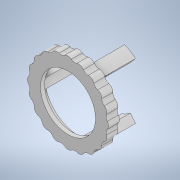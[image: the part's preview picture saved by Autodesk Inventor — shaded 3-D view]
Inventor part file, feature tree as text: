
AUTODESK INVENTOR PART (.ipt)
format: ipt  version: 2022 (Build 260153000, 153)  size: 384,512 bytes
history: native  units: in
note: dims shown in document units (in); Inventor stores cm internally (conversion verified against a paired STEP export)
features: thicken_offset x6, other x6, extrude x4, sketch x4, projected_geometry x4, plane x1, chamfer x1, fillet x1, reference x1
ambient origin geometry x8: Origin, YZ Plane, XZ Plane, XY Plane, X Axis, Y Axis, Z Axis, Center Point
bodies: Solid1 (feature_tree)
feature tree (28):
  extrude  "Extrusion1"  Depth=1.1681in
  plane  "Work Plane1"
  extrude  "Extrusion2"  Depth=0.481in
  extrude  "Extrusion3"  Depth=0.2in
  chamfer  "Chamfer1"  Distance=0.2in
  thicken_offset  "Thicken1"
  thicken_offset  "Thicken2"
  thicken_offset  "Thicken3"
  extrude  "Extrusion4"  Depth=0.6in TaperAngle=0.0deg
  fillet  "Fillet1"  Radius=1.315in
  thicken_offset  "Thicken4"
  thicken_offset  "Thicken5"
  thicken_offset  "Thicken6"
  sketch  "Sketch1"  dims[d0=1.1681in d1=1.1681in]
  reference  "Reference1"
  sketch  "Sketch3"  dims[d2=0.3436in d3=0.481in]
  sketch  "Sketch4"  dims[d4=0.3436in d5=0.481in d6=0.2in d7=0.0in]
  projected_geometry  "Projected Loop1"
  projected_geometry  "Projected Loop2"
  projected_geometry  "Projected Loop3"
  sketch  "Sketch5"  dims[d8=1.1681in d9=1.1681in d10=0.3436in d11=0.481in d12=0.3436in d13=0.481in d14=0.6in d15=0.0in d16=1.315in d17=1.025in d18=0.1181in d19=0.1181in d20=0.1181in d21=0.25in d22=0.0in d23=0.125in d24=0.125in d25=45.0deg d26=0.005in d27=0.005in d28=0.005in d29=0.005in d30=0.005in d31=0.005in d32=0.1in d33=135.0deg d34=45.0deg d35=7.874in d37=360.0deg d39=0.2in d40=0.0in d41=0.1in d42=0.01in d43=0.01in d44=0.01in d45=0.01in d46=0.01in d47=0.01in]
  projected_geometry  "Projected Loop4"
  parser-record x2  (decoder bookkeeping rows leaked as tree rows — omitted from the tree; the rows remain in map.json)
  other  "CubeAssembly.iam"
  other  "CubeFace:2"
  other  "Assembly1.iam"
  other  "CubeFace:1"
note: 2 file-system paths scrubbed to <path> (originals preserved in map.json)
